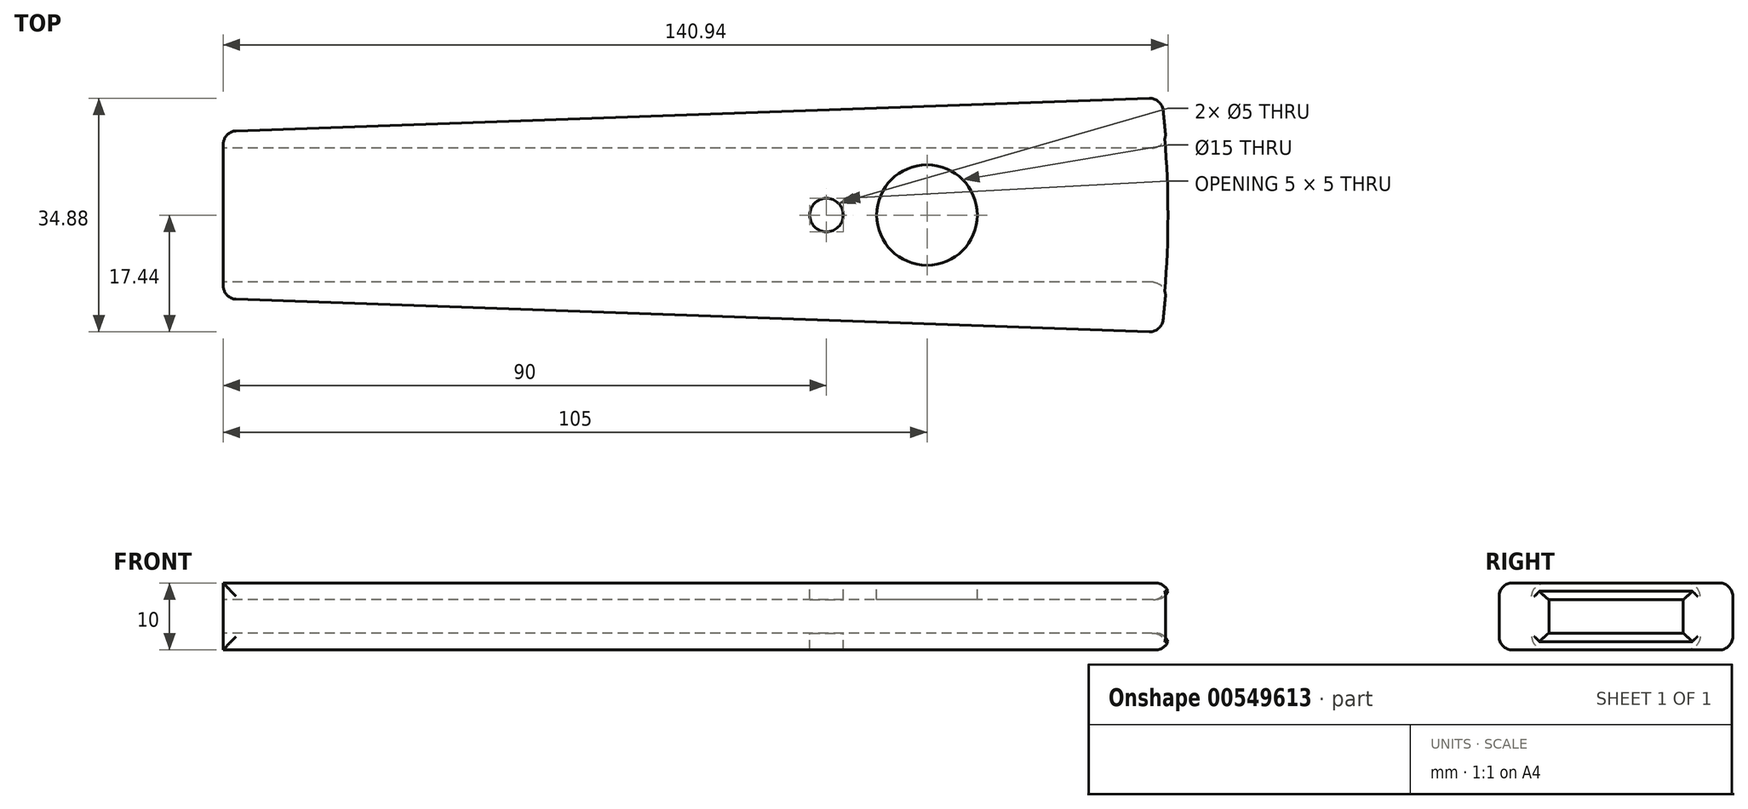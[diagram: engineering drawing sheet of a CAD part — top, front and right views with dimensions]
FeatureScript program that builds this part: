
annotation { "Feature Type Name" : "Feature", "Feature Type Description" : "" }
export const myFeature = defineFeature(function(context is Context, id is Id, definition is map)
    precondition{}
    {
        {
            var Q0;
            Q0=qCreatedBy(makeId("Top.planeOp"),FACE);
            var sketch = newSketch(context, id + "F0", { "sketchPlane" : qUnion([Q0])});
            skPoint(sketch, "E0", {"position": v(-70, 12.5) * mm});
            skPoint(sketch, "E1", {"position": v(-70, -12.5) * mm});
            skPoint(sketch, "E2", {"position": v(70, -17.5) * mm});
            skPoint(sketch, "E3", {"position": v(70, 17.5) * mm});
            skLineSegment(sketch, "E4", {"start": v(-70, 12.5) * mm, "end": v(-70, -12.5) * mm});
            skLineSegment(sketch, "E5", {"start": v(-70, -12.5) * mm, "end": v(70, -17.5) * mm});
            skLineSegment(sketch, "E6", {"start": v(-70, 12.5) * mm, "end": v(70, 17.5) * mm});
            skArc(sketch, "E7", {"start": v(70, -17.5) * mm, "mid": v(71.09, 0) * mm, "end": v(70, 17.5) * mm});
            skCircle(sketch, "E8", {"center": v(35, 0) * mm, "radius": 7.5 * mm});
            skSolve(sketch);
        }
        {
            var Q0;
            Q0=makeQuery(id+"F0.imprint","IMPRINT",FACE,{"disambiguationData":[TD([[makeQuery(id+"F0.imprint","IMPRINT",EDGE,{"derivedFrom":sQuery(id+"F0.wireOp",EDGE,"E4")}),1.0]])]});
            var Q1;
            Q1=makeQuery(id+"F0.imprint","IMPRINT",FACE,{"disambiguationData":[TD([[makeQuery(id+"F0.imprint","IMPRINT",EDGE,{"derivedFrom":sQuery(id+"F0.wireOp",EDGE,"E8")}),1.0]])]});
            extrude(context, id + "F1", {"entities" : qUnion([Q0, Q1]), "depth" : 10 * mm, "offsetDistance" : 25 * mm});
        }
        {
            var Q0;
            Q0=makeQuery(id+"F1.opExtrude","SWEPT_FACE",FACE,{"disambiguationData":[OSD([sQuery(id+"F0.wireOp",EDGE,"E4")])]});
            var sketch = newSketch(context, id + "F2", { "sketchPlane" : qUnion([Q0])});
            skLineSegment(sketch, "E9.bottom", {"start": v(-10, 7.5) * mm, "end": v(10, 7.5) * mm});
            skLineSegment(sketch, "E9.top", {"start": v(-10, 2.5) * mm, "end": v(10, 2.5) * mm});
            skLineSegment(sketch, "E9.left", {"start": v(-10, 7.5) * mm, "end": v(-10, 2.5) * mm});
            skLineSegment(sketch, "E9.right", {"start": v(10, 7.5) * mm, "end": v(10, 2.5) * mm});
            skSolve(sketch);
        }
        {
            var Q0;
            Q0=makeQuery(id+"F2.imprint","IMPRINT",FACE,{"disambiguationData":[TD([[makeQuery(id+"F2.imprint","IMPRINT",EDGE,{"derivedFrom":sQuery(id+"F2.wireOp",EDGE,"E9.bottom")}),-1.0]])]});
            extrude(context, id + "F3", {"entities" : qUnion([Q0]), "operationType" : NewBodyOperationType.REMOVE, "oppositeDirection" : true, "depth" : 200 * mm, "offsetDistance" : 25 * mm});
        }
        {
            var Q0;
            Q0=makeQuery(id+"F1.opExtrude","CAP_FACE",FACE,{"disambiguationData":[OSD([sQuery(id+"F0.wireOp",EDGE,"E4"),sQuery(id+"F0.wireOp",EDGE,"E5"),sQuery(id+"F0.wireOp",EDGE,"E6"),sQuery(id+"F0.wireOp",EDGE,"E7")])],"isStart":false});
            var sketch = newSketch(context, id + "F4", { "sketchPlane" : qUnion([Q0])});
            skCircle(sketch, "E10", {"center": v(35, 0) * mm, "radius": 7.5 * mm});
            skSolve(sketch);
        }
        {
            var Q0;
            Q0=makeQuery(id+"F4.imprint","IMPRINT",FACE,{"disambiguationData":[TD([[makeQuery(id+"F4.imprint","IMPRINT",EDGE,{"derivedFrom":sQuery(id+"F4.wireOp",EDGE,"E10")}),1.0]])]});
            extrude(context, id + "F5", {"entities" : qUnion([Q0]), "operationType" : NewBodyOperationType.REMOVE, "oppositeDirection" : true, "depth" : 2.5 * mm, "offsetDistance" : 25 * mm});
        }
        {
            var Q0;
            Q0=makeQuery(id+"F1.opExtrude","CAP_FACE",FACE,{"disambiguationData":[OSD([sQuery(id+"F0.wireOp",EDGE,"E4"),sQuery(id+"F0.wireOp",EDGE,"E5"),sQuery(id+"F0.wireOp",EDGE,"E6"),sQuery(id+"F0.wireOp",EDGE,"E7")])],"isStart":false});
            var sketch = newSketch(context, id + "F6", { "sketchPlane" : qUnion([Q0])});
            skCircle(sketch, "E11", {"center": v(20, 0) * mm, "radius": 2.5 * mm});
            skSolve(sketch);
        }
        {
            var Q0;
            Q0=makeQuery(id+"F6.imprint","IMPRINT",FACE,{"disambiguationData":[TD([[makeQuery(id+"F6.imprint","IMPRINT",EDGE,{"derivedFrom":sQuery(id+"F6.wireOp",EDGE,"E11")}),1.0]])]});
            extrude(context, id + "F7", {"entities" : qUnion([Q0]), "operationType" : NewBodyOperationType.REMOVE, "oppositeDirection" : true, "depth" : 10 * mm, "offsetDistance" : 25 * mm});
        }
        {
            var Q0;
            Q0=makeQuery(id+"F1.opExtrude","SWEPT_FACE",FACE,{"disambiguationData":[OSD([sQuery(id+"F0.wireOp",EDGE,"E5")])]});
            fillet(context, id + "F8", {"entities" : qUnion([Q0]), "radius" : 2 * mm, "tangentPropagation" : true, "allowEdgeOverflow" : false});
        }
        {
            var Q0;
            Q0=makeQuery(id+"F1.opExtrude","SWEPT_FACE",FACE,{"disambiguationData":[OSD([sQuery(id+"F0.wireOp",EDGE,"E7")])]});
            fillet(context, id + "F9", {"entities" : qUnion([Q0]), "radius" : 2 * mm, "tangentPropagation" : true, "allowEdgeOverflow" : false});
        }
        {
            var Q0;
            Q0=makeQuery(id+"F1.opExtrude","SWEPT_FACE",FACE,{"disambiguationData":[OSD([sQuery(id+"F0.wireOp",EDGE,"E6")])]});
            fillet(context, id + "F10", {"entities" : qUnion([Q0]), "radius" : 2 * mm, "tangentPropagation" : true, "allowEdgeOverflow" : false});
        }
    });
